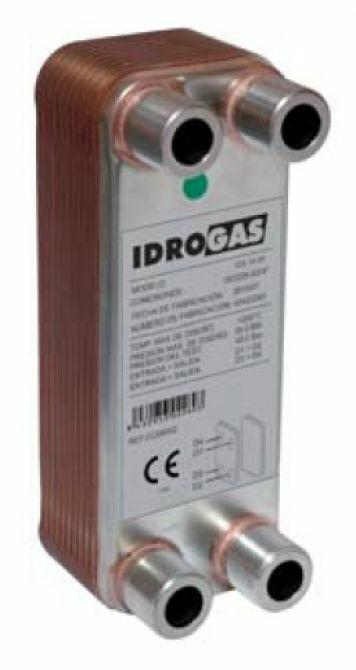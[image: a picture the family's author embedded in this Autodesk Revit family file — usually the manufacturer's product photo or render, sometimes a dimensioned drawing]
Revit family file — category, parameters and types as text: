
# Revit family: IDS110-40_CC08054
name_source: partatom
category: Aparatos eléctricos
revit_build: Autodesk Revit 2016 (Build: 20150220_1215(x64)
units: mm (PartAtom-declared; Revit-internal decimal feet)

## family parameters
Compartido = No
Corte con vacíos al cargar = No
Cota de conector redondo = Diámetro de uso
Mantener orientación de anotación = No
Número OmniClass = 23.80.00.00
Punto de cálculo de habitación = No
Se basa en plano de trabajo = No
Siempre vertical = Sí
Tipo de pieza = Caja de conexiones
Título OmniClass = Electric Power and Lighting

## types (1)
- IDS 110-40
    Caudal máx. = 34 m3/h
    Conexiones = 316L acero inox.
    Costo = 0 $
    Código de montaje = CC08054
    Descripción = INTERCAMBIADOR PLACAS TERMOSOLDADO
    Dimensiones = 616 x 191 x ~105 mm
    Fabricante = SALVADOR ESCODA
    Imagen de tipo = IDS-14.jpg
    Material soldadura = 99,99% cobre
    Modelo = IDS 110-40
    Peso = 21,4 Kg
    Placas = 316L acero inox.
    Placas cubierta = 304 acero inox.
    Presión trabajo = 0-30/45 bar
    Temperatura máx. trabajo = 225 ºC
    URL = www.salvadorescoda.com
